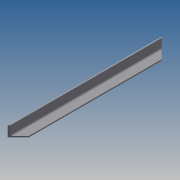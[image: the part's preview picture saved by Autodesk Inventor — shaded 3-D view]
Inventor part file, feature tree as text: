
AUTODESK INVENTOR PART (.ipt)
format: ipt  version: 2014 SP1 (Build 180222100, 222)  size: 90,624 bytes
history: native  units: in
note: dims shown in document units (in); Inventor stores cm internally (conversion verified against a paired STEP export)
features: extrude x2, sketch x2
ambient origin geometry x8: Origin, YZ Plane, XZ Plane, XY Plane, X Axis, Y Axis, Z Axis, Center Point
bodies: Solid1 (feature_tree)
feature tree (4):
  extrude  "Extrusion1"  Depth=1.0in
  extrude  "Extrusion8"  Depth=0.1476in
  sketch  "Sketch1"  dims[d0=1.0in d1=1.0in]
  sketch  "Sketch10"  dims[d2=0.1181in d3=0.1476in d4=14.7in d5=0.0in d36=45.0deg d37=45.0deg d38=2.0in d39=0.0in]
